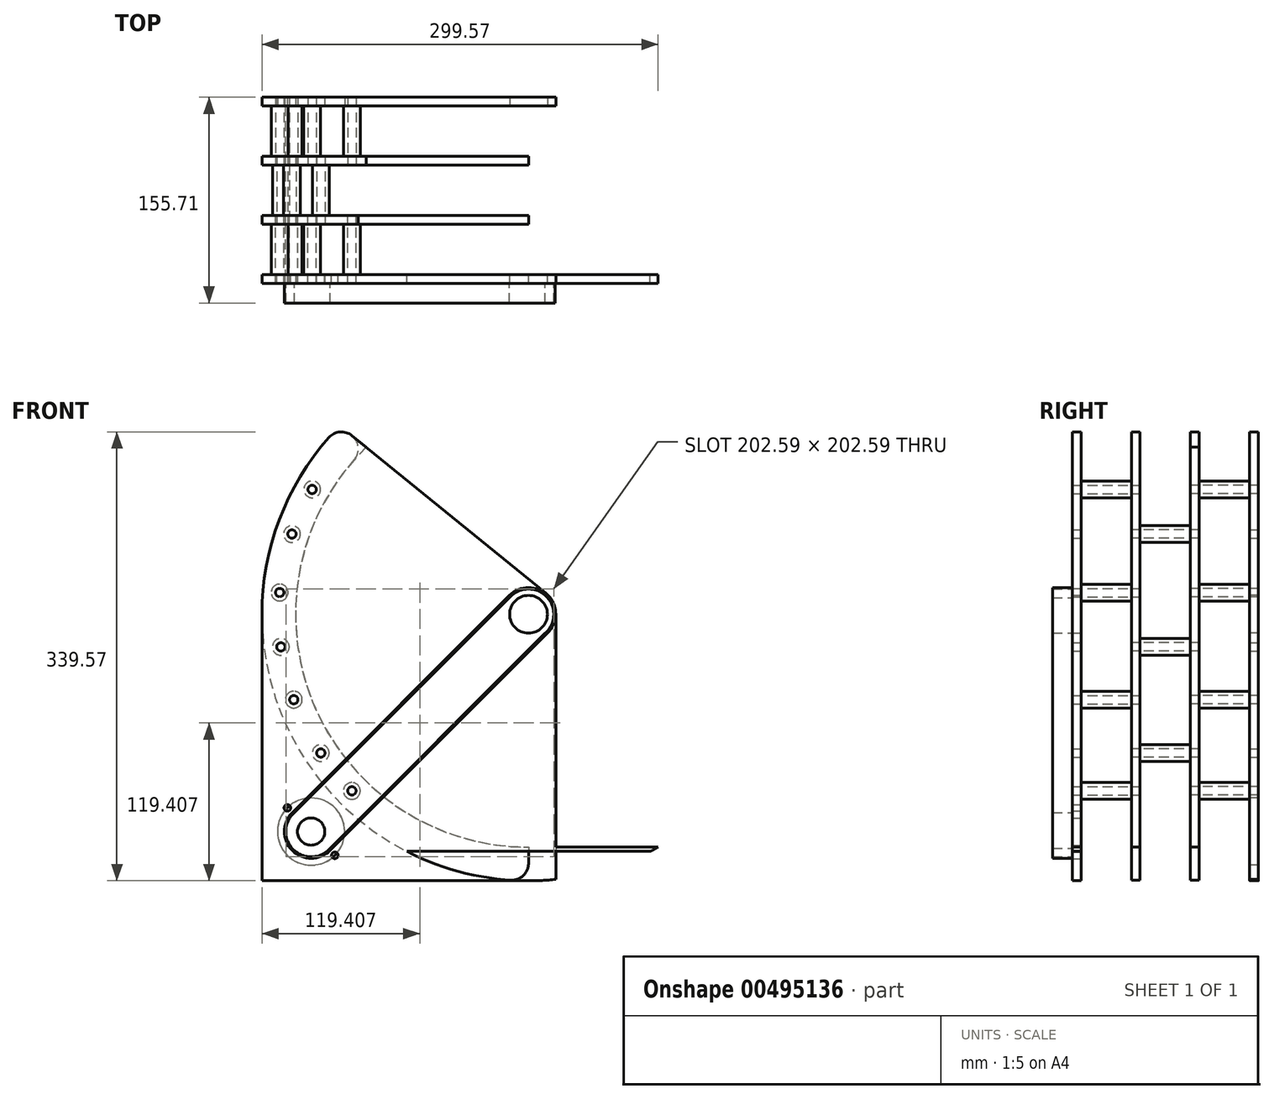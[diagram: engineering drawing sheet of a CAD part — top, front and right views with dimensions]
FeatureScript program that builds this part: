
annotation { "Feature Type Name" : "Feature", "Feature Type Description" : "" }
export const myFeature = defineFeature(function(context is Context, id is Id, definition is map)
    precondition{}
    {
        {
            var Q0;
            Q0=qCreatedBy(makeId("Front.planeOp"),FACE);
            var sketch = newSketch(context, id + "F0", { "sketchPlane" : qUnion([Q0])});
            skCircle(sketch, "E0", {"center": v(0, 0) * mm, "radius": 61.91 * mm});
            skCircle(sketch, "E1", {"center": v(0, 0) * mm, "radius": 176.21 * mm});
            skCircle(sketch, "E2.cCircle", {"center": v(0, 0) * mm, "radius": 6.35 * mm, "construction": true});
            skLineSegment(sketch, "E2.0", {"start": v(-3.67, 6.35) * mm, "end": v(3.67, 6.35) * mm});
            skLineSegment(sketch, "E2.1", {"start": v(3.67, 6.35) * mm, "end": v(7.33, 0) * mm});
            skLineSegment(sketch, "E2.2", {"start": v(7.33, 0) * mm, "end": v(3.67, -6.35) * mm});
            skLineSegment(sketch, "E2.3", {"start": v(3.67, -6.35) * mm, "end": v(-3.67, -6.35) * mm});
            skLineSegment(sketch, "E2.4", {"start": v(-3.67, -6.35) * mm, "end": v(-7.33, 0) * mm});
            skLineSegment(sketch, "E2.5", {"start": v(-7.33, 0) * mm, "end": v(-3.67, 6.35) * mm});
            skPoint(sketch, "E2.0.midPoint", {"position": v(0, 6.35) * mm});
            skCircle(sketch, "E3", {"center": v(0, 0) * mm, "radius": 201.61 * mm});
            skLineSegment(sketch, "E4", {"start": v(0, -176.21) * mm, "end": v(267.79, -176.21) * mm});
            skCircle(sketch, "E5", {"center": v(0, 0) * mm, "radius": 188.91 * mm, "construction": true});
            skCircle(sketch, "E6", {"center": v(-133.58, -133.58) * mm, "radius": 3.18 * mm});
            skLineSegment(sketch, "E7", {"start": v(0, 0) * mm, "end": v(-133.58, -133.58) * mm, "construction": true});
            skLineSegment(sketch, "E8", {"start": v(0, 0) * mm, "end": v(-142.56, 142.56) * mm});
            skCircle(sketch, "E9.1.0", {"center": v(-177.52, -64.61) * mm, "radius": 3.18 * mm});
            skCircle(sketch, "E9.2.0", {"center": v(-188.2, 16.46) * mm, "radius": 3.18 * mm});
            skCircle(sketch, "E9.3.0", {"center": v(-163.6, 94.46) * mm, "radius": 3.18 * mm});
            skLineSegment(sketch, "E9.anchor2", {"start": v(0, 0) * mm, "end": v(-163.6, 94.46) * mm, "construction": true});
            skLineSegment(sketch, "E10", {"start": v(267.83, -179.39) * mm, "end": v(-92.02, -179.39) * mm});
            skLineSegment(sketch, "E11", {"start": v(267.79, -176.21) * mm, "end": v(267.83, -179.39) * mm});
            skCircle(sketch, "E12", {"center": v(0, 0) * mm, "radius": 14.29 * mm});
            skCircle(sketch, "E13", {"center": v(0, 0) * mm, "radius": 20.64 * mm});
            skLineSegment(sketch, "E14", {"start": v(13.02, 16.01) * mm, "end": v(-142.56, 142.56) * mm});
            skLineSegment(sketch, "E15", {"start": v(20.64, 0) * mm, "end": v(20.64, -176.21) * mm});
            skLineSegment(sketch, "E16", {"start": v(20.64, -175.98) * mm, "end": v(20.64, -200.55) * mm});
            skLineSegment(sketch, "E17", {"start": v(-201.61, 0) * mm, "end": v(-201.61, -201.61) * mm});
            skLineSegment(sketch, "E18", {"start": v(-201.61, -201.61) * mm, "end": v(0, -201.61) * mm});
            skCircle(sketch, "E19", {"center": v(-164.4, -164.4) * mm, "radius": 10.32 * mm});
            skCircle(sketch, "E20", {"center": v(-146.44, -182.37) * mm, "radius": 2.49 * mm});
            skCircle(sketch, "E21", {"center": v(-182.37, -146.44) * mm, "radius": 2.49 * mm});
            skCircle(sketch, "E22", {"center": v(-164.4, -164.4) * mm, "radius": 25.4 * mm, "construction": true});
            skLineSegment(sketch, "E23", {"start": v(-146.44, -182.37) * mm, "end": v(-182.37, -146.44) * mm, "construction": true});
            skCircle(sketch, "E24", {"center": v(-164.4, -164.4) * mm, "radius": 19.1 * mm});
            skCircle(sketch, "E25", {"center": v(0, 0) * mm, "radius": 19.1 * mm});
            skLineSegment(sketch, "E26", {"start": v(-201.61, -201.61) * mm, "end": v(-133.58, -133.58) * mm, "construction": true});
            skSolve(sketch);
        }
        {
            var Q0;
            {var subQ0=sQuery(id+"F0.wireOp",EDGE,"E8");var subQ1=sQuery(id+"F0.wireOp",EDGE,"E0");var subQ2=makeQuery(id+"F0.imprint","INTERSECT",VERTEX,{"derivedFrom":[subQ1,subQ0]});Q0=makeQuery(id+"F0.imprint","IMPRINT",FACE,{"disambiguationData":[TD([[makeQuery(id+"F0.imprint","IMPRINT",EDGE,{"disambiguationData":[TD([[subQ2,1.0]])],"derivedFrom":subQ1}),1.0]])]});}
            var Q1;
            {var subQ0=sQuery(id+"F0.wireOp",EDGE,"E8");var subQ1=sQuery(id+"F0.wireOp",EDGE,"E0");var subQ2=makeQuery(id+"F0.imprint","INTERSECT",VERTEX,{"derivedFrom":[subQ1,subQ0]});Q1=makeQuery(id+"F0.imprint","IMPRINT",FACE,{"disambiguationData":[TD([[makeQuery(id+"F0.imprint","IMPRINT",EDGE,{"disambiguationData":[TD([[subQ2,1.0]])],"derivedFrom":subQ1}),-1.0]])]});}
            var Q2;
            {var subQ0=sQuery(id+"F0.wireOp",EDGE,"E8");var subQ1=sQuery(id+"F0.wireOp",EDGE,"E0");var subQ2=makeQuery(id+"F0.imprint","INTERSECT",VERTEX,{"derivedFrom":[subQ1,subQ0]});Q2=makeQuery(id+"F0.imprint","IMPRINT",FACE,{"disambiguationData":[TD([[makeQuery(id+"F0.imprint","IMPRINT",EDGE,{"disambiguationData":[TD([[subQ2,-1.0]])],"derivedFrom":subQ1}),-1.0]])]});}
            var Q3;
            {var subQ0=sQuery(id+"F0.wireOp",EDGE,"E8");var subQ1=sQuery(id+"F0.wireOp",EDGE,"E1");var subQ2=makeQuery(id+"F0.imprint","INTERSECT",VERTEX,{"derivedFrom":[subQ1,subQ0]});Q3=makeQuery(id+"F0.imprint","IMPRINT",FACE,{"disambiguationData":[TD([[makeQuery(id+"F0.imprint","IMPRINT",EDGE,{"disambiguationData":[TD([[subQ2,1.0]])],"derivedFrom":subQ1}),-1.0]])]});}
            var Q4;
            Q4=makeQuery(id+"F0.imprint","IMPRINT",FACE,{"disambiguationData":[TD([[makeQuery(id+"F0.imprint","IMPRINT",EDGE,{"derivedFrom":sQuery(id+"F0.wireOp",EDGE,"E12")}),-1.0]])]});
            var Q5;
            {var subQ0=sQuery(id+"F0.wireOp",EDGE,"E8");var subQ1=sQuery(id+"F0.wireOp",EDGE,"E0");var subQ2=makeQuery(id+"F0.imprint","INTERSECT",VERTEX,{"derivedFrom":[subQ1,subQ0]});Q5=makeQuery(id+"F0.imprint","IMPRINT",FACE,{"disambiguationData":[TD([[makeQuery(id+"F0.imprint","IMPRINT",EDGE,{"disambiguationData":[TD([[subQ2,-1.0]])],"derivedFrom":subQ1}),1.0]])]});}
            var Q6;
            {var subQ0=sQuery(id+"F0.wireOp",EDGE,"E4");var subQ1=sQuery(id+"F0.wireOp",EDGE,"E1");var subQ2=makeQuery(id+"F0.imprint","INTERSECT",VERTEX,{"derivedFrom":[subQ1,subQ0]});Q6=makeQuery(id+"F0.imprint","IMPRINT",FACE,{"disambiguationData":[TD([[makeQuery(id+"F0.imprint","IMPRINT",EDGE,{"disambiguationData":[TD([[subQ2,-1.0]])],"derivedFrom":subQ1}),-1.0]])]});}
            var Q7;
            {var subQ0=sQuery(id+"F0.wireOp",EDGE,"E10");var subQ1=sQuery(id+"F0.wireOp",EDGE,"E3");var subQ2=makeQuery(id+"F0.imprint","INTERSECT",VERTEX,{"disambiguationData":[OD(0.0)],"derivedFrom":[subQ1,subQ0]});Q7=makeQuery(id+"F0.imprint","IMPRINT",FACE,{"disambiguationData":[TD([[makeQuery(id+"F0.imprint","IMPRINT",EDGE,{"disambiguationData":[TD([[subQ2,-1.0]])],"derivedFrom":subQ1}),1.0]])]});}
            var Q8;
            Q8=makeQuery(id+"F0.imprint","IMPRINT",FACE,{"disambiguationData":[TD([[makeQuery(id+"F0.imprint","IMPRINT",EDGE,{"derivedFrom":sQuery(id+"F0.wireOp",EDGE,"E6")}),-1.0]])]});
            var Q9;
            Q9=makeQuery(id+"F0.imprint","IMPRINT",FACE,{"disambiguationData":[TD([[makeQuery(id+"F0.imprint","IMPRINT",EDGE,{"derivedFrom":sQuery(id+"F0.wireOp",EDGE,"E25")}),-1.0]])]});
            var Q10;
            {var subQ3=sQuery(id+"F0.wireOp",EDGE,"E17");Q10=makeQuery(id+"F0.imprint","IMPRINT",FACE,{"disambiguationData":[TD([[makeQuery(id+"F0.imprint","IMPRINT",EDGE,{"derivedFrom":subQ3}),1.0]])]});}
            var Q11;
            Q11=makeQuery(id+"F0.imprint","IMPRINT",FACE,{"disambiguationData":[TD([[makeQuery(id+"F0.imprint","IMPRINT",EDGE,{"derivedFrom":sQuery(id+"F0.wireOp",EDGE,"E19")}),-1.0]])]});
            extrude(context, id + "F1", {"entities" : qUnion([Q0, Q1, Q2, Q3, Q4, Q5, Q6, Q7, Q8, Q9, Q10, Q11]), "depth" : 6.6 * mm});
        }
        {
            var Q0;
            Q0=makeQuery(id+"F1.opExtrude","CAP_FACE",FACE,{"disambiguationData":[OSD([sQuery(id+"F0.wireOp",EDGE,"E1"),sQuery(id+"F0.wireOp",EDGE,"E3"),sQuery(id+"F0.wireOp",EDGE,"E4"),sQuery(id+"F0.wireOp",EDGE,"E6"),sQuery(id+"F0.wireOp",EDGE,"E8"),sQuery(id+"F0.wireOp",EDGE,"E9.1.0"),sQuery(id+"F0.wireOp",EDGE,"E9.2.0"),sQuery(id+"F0.wireOp",EDGE,"E9.3.0"),sQuery(id+"F0.wireOp",EDGE,"E10")])],"isStart":true});
            var sketch = newSketch(context, id + "F2", { "sketchPlane" : qUnion([Q0])});
            skCircle(sketch, "E27", {"center": v(163.6, 94.46) * mm, "radius": 6.35 * mm});
            skCircle(sketch, "E28", {"center": v(188.2, 16.46) * mm, "radius": 6.35 * mm});
            skCircle(sketch, "E29", {"center": v(177.52, -64.61) * mm, "radius": 6.35 * mm});
            skCircle(sketch, "E30", {"center": v(133.58, -133.58) * mm, "radius": 6.35 * mm});
            skSolve(sketch);
        }
        {
            var Q0;
            Q0=qSketchRegion(id+"F2",true);
            extrude(context, id + "F3", {"entities" : qUnion([Q0]), "operationType" : NewBodyOperationType.ADD, "depth" : 38.1 * mm});
        }
        {
            var Q0;
            Q0=makeQuery(id+"F3.opExtrude","CAP_FACE",FACE,{"disambiguationData":[OSD([sQuery(id+"F2.wireOp",EDGE,"E27")])],"isStart":false});
            var sketch = newSketch(context, id + "F4", { "sketchPlane" : qUnion([Q0])});
            skCircle(sketch, "E31", {"center": v(0, 0) * mm, "radius": 201.61 * mm});
            skCircle(sketch, "E32", {"center": v(0, 0) * mm, "radius": 176.21 * mm});
            skCircle(sketch, "E33", {"center": v(133.58, 133.58) * mm, "radius": 6.35 * mm});
            skLineSegment(sketch, "E34", {"start": v(133.58, 133.58) * mm, "end": v(0, 0) * mm, "construction": true});
            skCircle(sketch, "E35", {"center": v(0, 0) * mm, "radius": 188.91 * mm, "construction": true});
            skCircle(sketch, "E36.1.0", {"center": v(178.89, 60.72) * mm, "radius": 6.35 * mm});
            skCircle(sketch, "E36.2.0", {"center": v(187.3, -24.66) * mm, "radius": 6.35 * mm});
            skCircle(sketch, "E36.3.0", {"center": v(157.08, -104.95) * mm, "radius": 6.35 * mm});
            skCircle(sketch, "E36.4.0", {"center": v(94.46, -163.6) * mm, "radius": 6.35 * mm});
            skLineSegment(sketch, "E36.anchor1", {"start": v(0, 0) * mm, "end": v(133.58, 133.58) * mm, "construction": true});
            skLineSegment(sketch, "E36.anchor2", {"start": v(0, 0) * mm, "end": v(94.46, -163.6) * mm, "construction": true});
            skLineSegment(sketch, "E37.0", {"start": v(-13.02, 16.01) * mm, "end": v(142.56, 142.56) * mm});
            skCircle(sketch, "E38", {"center": v(163.6, 94.46) * mm, "radius": 3.18 * mm});
            skCircle(sketch, "E39", {"center": v(178.89, 60.72) * mm, "radius": 3.18 * mm});
            skCircle(sketch, "E40", {"center": v(188.2, 16.46) * mm, "radius": 3.18 * mm});
            skCircle(sketch, "E41", {"center": v(187.3, -24.66) * mm, "radius": 3.18 * mm});
            skCircle(sketch, "E42", {"center": v(177.52, -64.61) * mm, "radius": 3.18 * mm});
            skCircle(sketch, "E43", {"center": v(157.08, -104.95) * mm, "radius": 3.18 * mm});
            skCircle(sketch, "E44", {"center": v(133.58, -133.58) * mm, "radius": 3.18 * mm});
            skLineSegment(sketch, "E45", {"start": v(0, 0) * mm, "end": v(0, -201.61) * mm});
            skSolve(sketch);
        }
        {
            var Q0;
            {var subQ0=sQuery(id+"F4.wireOp",EDGE,"E37.0");var subQ1=sQuery(id+"F4.wireOp",EDGE,"E33");var subQ2=makeQuery(id+"F4.imprint","INTERSECT",VERTEX,{"disambiguationData":[OD(0.0)],"derivedFrom":[subQ1,subQ0]});Q0=makeQuery(id+"F4.imprint","IMPRINT",FACE,{"disambiguationData":[TD([[makeQuery(id+"F4.imprint","IMPRINT",EDGE,{"disambiguationData":[TD([[subQ2,-1.0]])],"derivedFrom":subQ1}),1.0]])]});}
            var Q1;
            Q1=makeQuery(id+"F4.imprint","IMPRINT",FACE,{"disambiguationData":[TD([[makeQuery(id+"F4.imprint","IMPRINT",EDGE,{"derivedFrom":sQuery(id+"F4.wireOp",EDGE,"E36.1.0")}),-1.0]])]});
            var Q2;
            Q2=makeQuery(id+"F4.imprint","IMPRINT",FACE,{"disambiguationData":[TD([[makeQuery(id+"F4.imprint","IMPRINT",EDGE,{"derivedFrom":sQuery(id+"F4.wireOp",EDGE,"E38")}),-1.0]])]});
            var Q3;
            Q3=makeQuery(id+"F4.imprint","IMPRINT",FACE,{"disambiguationData":[TD([[makeQuery(id+"F4.imprint","IMPRINT",EDGE,{"derivedFrom":sQuery(id+"F4.wireOp",EDGE,"E36.1.0")}),1.0]])]});
            var Q4;
            Q4=makeQuery(id+"F4.imprint","IMPRINT",FACE,{"disambiguationData":[TD([[makeQuery(id+"F4.imprint","IMPRINT",EDGE,{"derivedFrom":sQuery(id+"F4.wireOp",EDGE,"E36.2.0")}),1.0]])]});
            var Q5;
            Q5=makeQuery(id+"F4.imprint","IMPRINT",FACE,{"disambiguationData":[TD([[makeQuery(id+"F4.imprint","IMPRINT",EDGE,{"derivedFrom":sQuery(id+"F4.wireOp",EDGE,"E36.3.0")}),1.0]])]});
            var Q6;
            Q6=makeQuery(id+"F4.imprint","IMPRINT",FACE,{"disambiguationData":[TD([[makeQuery(id+"F4.imprint","IMPRINT",EDGE,{"derivedFrom":sQuery(id+"F4.wireOp",EDGE,"E36.4.0")}),1.0]])]});
            extrude(context, id + "F5", {"entities" : qUnion([Q0, Q1, Q2, Q3, Q4, Q5, Q6]), "operationType" : NewBodyOperationType.ADD, "depth" : 6.6 * mm});
        }
        {
            var Q0;
            Q0=makeQuery(id+"F5.opExtrude","CAP_FACE",FACE,{"disambiguationData":[OSD([sQuery(id+"F4.wireOp",EDGE,"E31"),sQuery(id+"F4.wireOp",EDGE,"E32"),sQuery(id+"F4.wireOp",EDGE,"E37.0"),sQuery(id+"F4.wireOp",EDGE,"E38"),sQuery(id+"F4.wireOp",EDGE,"E39"),sQuery(id+"F4.wireOp",EDGE,"E40"),sQuery(id+"F4.wireOp",EDGE,"E41"),sQuery(id+"F4.wireOp",EDGE,"E42"),sQuery(id+"F4.wireOp",EDGE,"E43"),sQuery(id+"F4.wireOp",EDGE,"E44"),sQuery(id+"F4.wireOp",EDGE,"E45")])],"isStart":false});
            var sketch = newSketch(context, id + "F6", { "sketchPlane" : qUnion([Q0])});
            skCircle(sketch, "E46", {"center": v(178.89, 60.72) * mm, "radius": 6.35 * mm});
            skCircle(sketch, "E47", {"center": v(187.3, -24.66) * mm, "radius": 6.35 * mm});
            skCircle(sketch, "E48", {"center": v(157.08, -104.95) * mm, "radius": 6.35 * mm});
            skSolve(sketch);
        }
        {
            var Q0;
            Q0=qSketchRegion(id+"F6",true);
            extrude(context, id + "F7", {"entities" : qUnion([Q0]), "operationType" : NewBodyOperationType.ADD, "depth" : 38.1 * mm});
        }
        {
            var Q0;
            Q0=makeQuery(id+"F7.opExtrude","CAP_FACE",FACE,{"disambiguationData":[OSD([sQuery(id+"F6.wireOp",EDGE,"E46")])],"isStart":false});
            var sketch = newSketch(context, id + "F8", { "sketchPlane" : qUnion([Q0])});
            skCircle(sketch, "E49.0", {"center": v(163.6, 94.46) * mm, "radius": 3.18 * mm});
            skArc(sketch, "E50.1", {"start": v(0, -176.21) * mm, "mid": v(163.3, -66.22) * mm, "end": v(122.74, 126.44) * mm});
            skPoint(sketch, "E51.0", {"position": v(132.65, 134.5) * mm});
            skLineSegment(sketch, "E52.0", {"start": v(122.74, 126.44) * mm, "end": v(142.56, 142.56) * mm});
            skLineSegment(sketch, "E53.0.0", {"start": v(142.56, 142.56) * mm, "end": v(122.74, 126.44) * mm});
            skArc(sketch, "E53.0.1", {"start": v(122.74, 126.44) * mm, "mid": v(163.3, -66.22) * mm, "end": v(0, -176.21) * mm});
            skLineSegment(sketch, "E53.0.2", {"start": v(0, -176.21) * mm, "end": v(0, -201.61) * mm});
            skArc(sketch, "E53.0.3", {"start": v(0, -201.61) * mm, "mid": v(186.27, -77.15) * mm, "end": v(142.56, 142.56) * mm});
            skCircle(sketch, "E54.0", {"center": v(188.2, 16.46) * mm, "radius": 3.18 * mm});
            skCircle(sketch, "E55.0", {"center": v(177.52, -64.61) * mm, "radius": 3.18 * mm});
            skCircle(sketch, "E56.0", {"center": v(133.58, -133.58) * mm, "radius": 3.18 * mm});
            skCircle(sketch, "E57.0", {"center": v(157.08, -104.95) * mm, "radius": 3.18 * mm});
            skCircle(sketch, "E58.0", {"center": v(187.3, -24.66) * mm, "radius": 3.18 * mm});
            skCircle(sketch, "E59.0", {"center": v(178.89, 60.72) * mm, "radius": 3.18 * mm});
            skSolve(sketch);
        }
        {
            var Q0;
            Q0=qSketchRegion(id+"F8",true);
            extrude(context, id + "F9", {"entities" : qUnion([Q0]), "operationType" : NewBodyOperationType.ADD, "depth" : 6.6 * mm});
        }
        {
            var Q0;
            Q0=makeQuery(id+"F9.opExtrude","CAP_FACE",FACE,{"disambiguationData":[OSD([sQuery(id+"F8.wireOp",EDGE,"E49.0"),sQuery(id+"F8.wireOp",EDGE,"E53.0.0"),sQuery(id+"F8.wireOp",EDGE,"E53.0.1"),sQuery(id+"F8.wireOp",EDGE,"E53.0.2"),sQuery(id+"F8.wireOp",EDGE,"E53.0.3"),sQuery(id+"F8.wireOp",EDGE,"E54.0"),sQuery(id+"F8.wireOp",EDGE,"E55.0"),sQuery(id+"F8.wireOp",EDGE,"E56.0"),sQuery(id+"F8.wireOp",EDGE,"E57.0"),sQuery(id+"F8.wireOp",EDGE,"E58.0"),sQuery(id+"F8.wireOp",EDGE,"E59.0")])],"isStart":false});
            var sketch = newSketch(context, id + "F10", { "sketchPlane" : qUnion([Q0])});
            skCircle(sketch, "E60.0", {"center": v(163.6, 94.46) * mm, "radius": 6.35 * mm});
            skCircle(sketch, "E61.0", {"center": v(188.2, 16.46) * mm, "radius": 6.35 * mm});
            skCircle(sketch, "E62.1", {"center": v(177.52, -64.61) * mm, "radius": 6.35 * mm});
            skCircle(sketch, "E63.0", {"center": v(133.58, -133.58) * mm, "radius": 6.35 * mm});
            skSolve(sketch);
        }
        {
            var Q0;
            Q0=qSketchRegion(id+"F10",true);
            extrude(context, id + "F11", {"entities" : qUnion([Q0]), "operationType" : NewBodyOperationType.ADD, "depth" : 38.1 * mm});
        }
        {
            var Q0;
            Q0=makeQuery(id+"F11.opExtrude","CAP_FACE",FACE,{"disambiguationData":[OSD([sQuery(id+"F10.wireOp",EDGE,"E60.0")])],"isStart":false});
            var sketch = newSketch(context, id + "F12", { "sketchPlane" : qUnion([Q0])});
            skLineSegment(sketch, "E64.0", {"start": v(-13.02, 16.01) * mm, "end": v(142.56, 142.56) * mm});
            skArc(sketch, "E65.0", {"start": v(-20.64, 0) * mm, "mid": v(-18.64, 8.86) * mm, "end": v(-13.02, 16.01) * mm});
            skLineSegment(sketch, "E66.0", {"start": v(-20.64, 0) * mm, "end": v(-20.64, -176.21) * mm});
            skCircle(sketch, "E67.0", {"center": v(0, 0) * mm, "radius": 14.29 * mm});
            skCircle(sketch, "E68.0", {"center": v(163.6, 94.46) * mm, "radius": 3.18 * mm});
            skCircle(sketch, "E69.0", {"center": v(188.2, 16.46) * mm, "radius": 3.18 * mm});
            skCircle(sketch, "E70.0", {"center": v(177.52, -64.61) * mm, "radius": 3.18 * mm});
            skCircle(sketch, "E71.0", {"center": v(133.58, -133.58) * mm, "radius": 3.18 * mm});
            skLineSegment(sketch, "E72.0", {"start": v(-20.64, -176.21) * mm, "end": v(-20.64, -176.21) * mm});
            skLineSegment(sketch, "E73", {"start": v(-20.64, -176.21) * mm, "end": v(-20.64, -200.55) * mm});
            skLineSegment(sketch, "E74.0", {"start": v(201.61, 0) * mm, "end": v(201.61, -201.61) * mm});
            skLineSegment(sketch, "E75.0", {"start": v(201.61, -201.61) * mm, "end": v(0, -201.61) * mm});
            skArc(sketch, "E76.0", {"start": v(0, -201.61) * mm, "mid": v(-10.33, -201.35) * mm, "end": v(-20.64, -200.55) * mm});
            skArc(sketch, "E77.0", {"start": v(142.56, 142.56) * mm, "mid": v(186.27, 77.15) * mm, "end": v(201.61, 0) * mm});
            skCircle(sketch, "E78.0", {"center": v(164.4, -164.4) * mm, "radius": 10.32 * mm});
            skCircle(sketch, "E79", {"center": v(164.4, -164.4) * mm, "radius": 25.4 * mm});
            skSolve(sketch);
        }
        {
            var Q0;
            Q0=qSketchRegion(id+"F12",true);
            extrude(context, id + "F13", {"entities" : qUnion([Q0]), "operationType" : NewBodyOperationType.ADD, "depth" : 6.6 * mm});
        }
        {
            var Q0;
            Q0=makeQuery(id+"F13.opExtrude","CAP_FACE",FACE,{"disambiguationData":[OSD([sQuery(id+"F12.wireOp",EDGE,"E64.0"),sQuery(id+"F12.wireOp",EDGE,"E65.0"),sQuery(id+"F12.wireOp",EDGE,"E66.0"),sQuery(id+"F12.wireOp",EDGE,"E67.0"),sQuery(id+"F12.wireOp",EDGE,"730f6a13-53ba-409a-a2d9-1ac5f82f5084.0"),sQuery(id+"F12.wireOp",EDGE,"E68.0"),sQuery(id+"F12.wireOp",EDGE,"E69.0"),sQuery(id+"F12.wireOp",EDGE,"E70.0"),sQuery(id+"F12.wireOp",EDGE,"E71.0"),sQuery(id+"F12.wireOp",EDGE,"E73")])],"isStart":false});
            var sketch = newSketch(context, id + "F14", { "sketchPlane" : qUnion([Q0])});
            skCircle(sketch, "E80.0", {"center": v(163.6, 94.46) * mm, "radius": 3.18 * mm});
            skCircle(sketch, "E81.0", {"center": v(188.2, 16.46) * mm, "radius": 3.18 * mm});
            skCircle(sketch, "E82.0", {"center": v(177.52, -64.61) * mm, "radius": 3.18 * mm});
            skCircle(sketch, "E83.0", {"center": v(133.58, -133.58) * mm, "radius": 3.18 * mm});
            skCircle(sketch, "E84.0", {"center": v(157.08, -104.95) * mm, "radius": 3.18 * mm});
            skCircle(sketch, "E85.0", {"center": v(187.3, -24.66) * mm, "radius": 3.18 * mm});
            skCircle(sketch, "E86.0", {"center": v(178.89, 60.72) * mm, "radius": 3.18 * mm});
            skSolve(sketch);
        }
        {
            var Q0;
            Q0=qSketchRegion(id+"F14",true);
            extrude(context, id + "F15", {"entities" : qUnion([Q0]), "operationType" : NewBodyOperationType.REMOVE, "endBound" : BoundingType.THROUGH_ALL, "oppositeDirection" : true, "depth" : 25.4 * mm});
        }
        {
            var Q0;
            Q0=makeQuery(id+"F1.opExtrude","SWEPT_EDGE",EDGE,{"disambiguationData":[OSD([sQuery(id+"F0.wireOp",EDGE,"E3"),sQuery(id+"F0.wireOp",EDGE,"E8"),sQuery(id+"F0.wireOp",EDGE,"E14")])]});
            var Q1;
            Q1=makeQuery(id+"F5.opExtrude","SWEPT_EDGE",EDGE,{"disambiguationData":[OSD([sQuery(id+"F4.wireOp",EDGE,"E31"),sQuery(id+"F4.wireOp",EDGE,"E37.0")])]});
            var Q2;
            Q2=makeQuery(id+"F9.opExtrude","SWEPT_EDGE",EDGE,{"disambiguationData":[OSD([sQuery(id+"F8.wireOp",EDGE,"E53.0.0"),sQuery(id+"F8.wireOp",EDGE,"E53.0.1")])]});
            var Q3;
            Q3=makeQuery(id+"F9.opExtrude","SWEPT_EDGE",EDGE,{"disambiguationData":[OSD([sQuery(id+"F8.wireOp",EDGE,"E53.0.0"),sQuery(id+"F8.wireOp",EDGE,"E53.0.3")])]});
            var Q4;
            Q4=makeQuery(id+"F5.opExtrude","SWEPT_EDGE",EDGE,{"disambiguationData":[OSD([sQuery(id+"F4.wireOp",EDGE,"E32"),sQuery(id+"F4.wireOp",EDGE,"E37.0")])]});
            var Q5;
            Q5=makeQuery(id+"F13.opExtrude","SWEPT_EDGE",EDGE,{"disambiguationData":[OSD([sQuery(id+"F12.wireOp",EDGE,"E64.0"),sQuery(id+"F12.wireOp",EDGE,"E77.0")])]});
            var Q6;
            Q6=makeQuery(id+"F5.opExtrude","SWEPT_EDGE",EDGE,{"disambiguationData":[OSD([sQuery(id+"F4.wireOp",EDGE,"E31"),sQuery(id+"F4.wireOp",EDGE,"E45")])]});
            var Q7;
            Q7=makeQuery(id+"F9.opExtrude","SWEPT_EDGE",EDGE,{"disambiguationData":[OSD([sQuery(id+"F8.wireOp",EDGE,"E53.0.2"),sQuery(id+"F8.wireOp",EDGE,"E53.0.3")])]});
            fillet(context, id + "F16", {"entities" : qUnion([Q0, Q1, Q2, Q3, Q4, Q5, Q6, Q7]), "radius" : 12.7 * mm, "tangentPropagation" : true, "allowEdgeOverflow" : false});
        }
        {
            var Q0;
            Q0=makeQuery(id+"F1.opExtrude","CAP_FACE",FACE,{"disambiguationData":[OSD([sQuery(id+"F0.wireOp",EDGE,"E3"),sQuery(id+"F0.wireOp",EDGE,"E4"),sQuery(id+"F0.wireOp",EDGE,"E6"),sQuery(id+"F0.wireOp",EDGE,"E9.1.0"),sQuery(id+"F0.wireOp",EDGE,"E9.2.0"),sQuery(id+"F0.wireOp",EDGE,"E9.3.0"),sQuery(id+"F0.wireOp",EDGE,"E12"),sQuery(id+"F0.wireOp",EDGE,"E13"),sQuery(id+"F0.wireOp",EDGE,"E14"),sQuery(id+"F0.wireOp",EDGE,"E15"),sQuery(id+"F0.wireOp",EDGE,"E16"),sQuery(id+"F0.wireOp",EDGE,"E17"),sQuery(id+"F0.wireOp",EDGE,"E18"),sQuery(id+"F0.wireOp",EDGE,"E19"),sQuery(id+"F0.wireOp",EDGE,"E20"),sQuery(id+"F0.wireOp",EDGE,"E21")])],"isStart":false});
            var sketch = newSketch(context, id + "F17", { "sketchPlane" : qUnion([Q0])});
            skCircle(sketch, "E87.0", {"center": v(0, 0) * mm, "radius": 19.1 * mm});
            skCircle(sketch, "E88.0", {"center": v(-164.4, -164.4) * mm, "radius": 19.1 * mm});
            skCircle(sketch, "E89", {"center": v(-164.4, -164.4) * mm, "radius": 20.24 * mm});
            skCircle(sketch, "E90", {"center": v(0, 0) * mm, "radius": 20.24 * mm});
            skLineSegment(sketch, "E91", {"start": v(-178.72, -150.1) * mm, "end": v(-14.31, 14.31) * mm});
            skLineSegment(sketch, "E92", {"start": v(-177.05, -150.1) * mm, "end": v(-14.31, 12.65) * mm});
            skLineSegment(sketch, "E93.MirrorCS", {"start": v(-150.1, -178.72) * mm, "end": v(14.31, -14.31) * mm});
            skLineSegment(sketch, "E94.MirrorCS", {"start": v(-150.1, -177.05) * mm, "end": v(12.65, -14.31) * mm});
            skSolve(sketch);
        }
        {
            var Q0;
            Q0=qSketchRegion(id+"F17",true);
            extrude(context, id + "F18", {"entities" : qUnion([Q0]), "depth" : 15 * mm});
        }
    });
